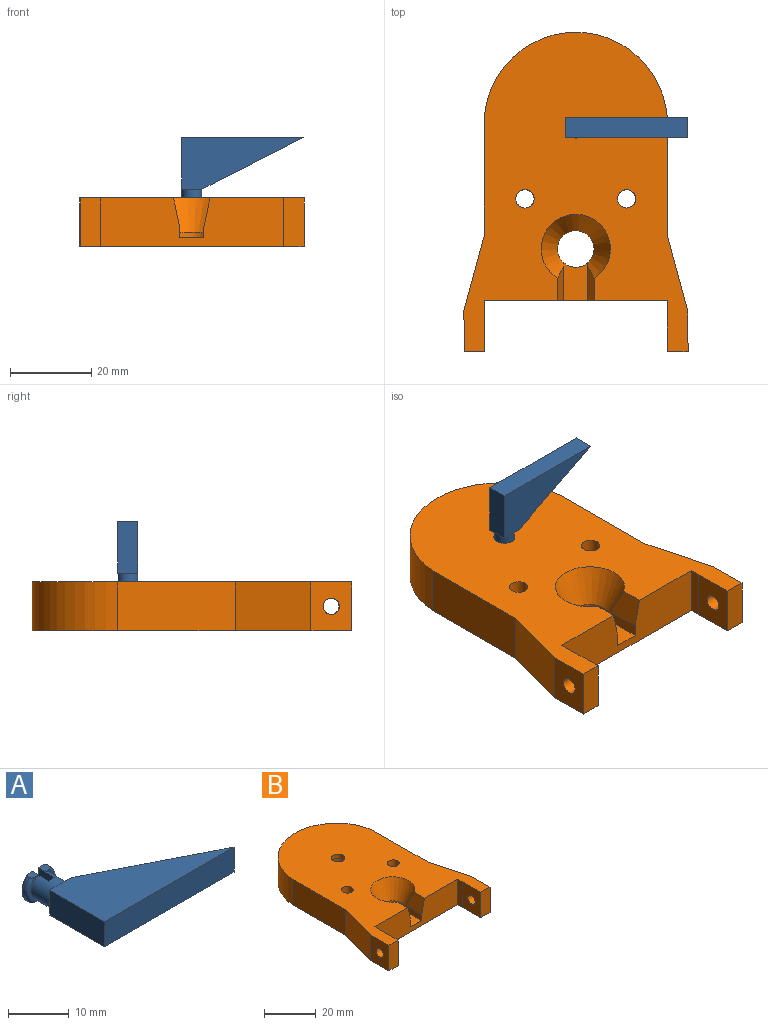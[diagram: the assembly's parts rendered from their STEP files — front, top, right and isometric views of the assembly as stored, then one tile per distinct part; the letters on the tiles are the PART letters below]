
ASSEMBLY  parts=2 mates=1
PART A: 27 faces, bbox 31.2x18.6x6.3 mm
  f0: plane 5x2.2mm, normal (0,1,0), area 8.9mm2, adj f7,f19,f21,f25
  f1: cylinder r=3.4mm len=5mm, axis (0,1,0), area 2.8mm2, adj f20,f22,f23,f24
  f2: plane 5x2.2mm, normal (0,-1,0), area 2.6mm2, adj f6,f8,f20,f22,f23
  f3: plane 5x2.2mm, normal (0,1,0), area 8.9mm2, adj f6,f20,f22,f24
  f4: cylinder r=3.4mm len=5mm, axis (0,1,0), area 2.8mm2, adj f19,f21,f25,f26
  f5: plane 5x2.2mm, normal (0,-1,0), area 2.6mm2, adj f7,f8,f19,f21,f26
  f6: plane 5x3.79mm, normal (1,0,0), area 18.5mm2, adj f2,f3,f8,f18,f20,f22
  f7: plane 5x3.79mm, normal (-1,0,0), area 18.5mm2, adj f0,f5,f8,f18,f19,f21
  f8: cylinder r=2.5mm len=5mm, axis (0,1,0), area 61mm2, adj f2,f5,f6,f7,f9,f10,f11,f12
  f9: plane 2.5x2.5mm, normal (0,1,0), area 1.3mm2, adj f8,f13,f16
  f10: plane 2.5x2.5mm, normal (0,1,0), area 1.3mm2, adj f8,f15,f16
  f11: plane 2.5x2.5mm, normal (0,1,0), area 1.3mm2, adj f8,f15,f17
  f12: plane 2.5x2.5mm, normal (0,1,0), area 1.3mm2, adj f8,f13,f17
  f13: plane 12.77x5mm, normal (-1,0,0), area 63.8mm2, adj f9,f12,f14,f16,f17
  f14: plane 30x5mm, normal (0,-1,0), area 150mm2, adj f13,f15,f16,f17
  f15: plane 25x12.77mm, normal (0.45,0.89,0), area 140.4mm2, adj f10,f11,f14,f16,f17
  f16: plane 30x12.77mm, normal (0,0,1), area 223.4mm2, adj f9,f10,f13,f14,f15
  f17: plane 30x12.77mm, normal (0,0,-1), area 223.4mm2, adj f11,f12,f13,f14,f15
  f18: plane 5x1.4mm, normal (0,1,0), area 6.9mm2, adj f6,f7,f8
  f19: plane 1.61x1.49mm, normal (0,0,1), area 2.2mm2, adj f0,f4,f5,f7,f25,f26
  f20: plane 1.61x1.49mm, normal (0,0,1), area 2.2mm2, adj f1,f2,f3,f6,f23,f24
  f21: plane 1.61x1.49mm, normal (0,0,-1), area 2.2mm2, adj f0,f4,f5,f7,f25,f26
  f22: plane 1.61x1.49mm, normal (0,0,-1), area 2.2mm2, adj f1,f2,f3,f6,f23,f24
  f23: torus R=2.9mm, axis (0,1,0), area 4.5mm2, adj f1,f2,f20,f22
  f24: torus R=2.9mm, axis (0,1,0), area 4.5mm2, adj f1,f3,f20,f22
  f25: torus R=2.9mm, axis (0,1,0), area 4.5mm2, adj f0,f4,f19,f21
  f26: torus R=2.9mm, axis (0,1,0), area 4.5mm2, adj f4,f5,f19,f21
PART B: 31 faces, bbox 55.2x78.6x12.1 mm
  f0: plane 28.92x12mm, normal (1,0,0), area 347mm2, adj f6,f7,f13,f15
  f1: plane 28.92x12mm, normal (-1,0,0), area 347mm2, adj f6,f7,f12,f15
  f2: plane 9.4x2.85mm, normal (1,0,0), area 25.5mm2, adj f3,f5,f8,f9,f16
  f3: cylinder r=4.5mm len=9mm, axis (0,0,-1), area 90.4mm2, adj f2,f4,f7,f8,f16
  f4: plane 9.4x2.85mm, normal (-1,0,0), area 25.5mm2, adj f3,f5,f8,f10,f16
  f5: plane 45x12mm, normal (0,-1,0), area 470.7mm2, adj f2,f4,f6,f7,f8,f9,f10,f11
  f6: plane 78.51x55.12mm, normal (0,0,1), area 2624.7mm2, adj f0,f1,f5,f9,f10,f11,f12,f13
  f7: plane 78.51x55.12mm, normal (0,0,-1), area 2850mm2, adj f0,f1,f3,f5,f11,f12,f13,f14
  f8: plane 9.35x6mm, normal (0,0,1), area 51.4mm2, adj f2,f3,f4,f5
  f9: plane 8.54x7.1mm, normal (0.98,0,0.21), area 49.9mm2, adj f2,f5,f6,f16
  f10: plane 8.54x7.1mm, normal (-0.98,0,0.21), area 49.9mm2, adj f4,f5,f6,f16
  f11: plane 12x2.5mm, normal (1,0,0), area 30mm2, adj f5,f6,f7,f18
  f12: plane 18.64x12mm, normal (-0.97,0.26,0), area 231.6mm2, adj f1,f6,f7,f17
  f13: plane 18.64x12mm, normal (0.97,0.26,0), area 231.6mm2, adj f0,f6,f7,f21
  f14: plane 12x2.5mm, normal (-1,0,0), area 30mm2, adj f5,f6,f7,f20
  f15: cylinder r=22.56mm len=45mm, axis (0,0,-1), area 812mm2, adj f0,f1,f6,f7
  f16: cone r=4.5mm half-angle=25.2deg, axis (0,0,1), area 311mm2, adj f2,f3,f4,f6,f9,f10
  f17: plane 12x10mm, normal (-1,-0.01,0), area 107.4mm2, adj f6,f7,f12,f19,f23
  f18: plane 12x10mm, normal (1,0.01,0), area 107.4mm2, adj f6,f7,f11,f19,f23
  f19: plane 12x5.01mm, normal (0.01,-1,0), area 60.1mm2, adj f6,f7,f17,f18
  f20: plane 12x10mm, normal (-1,-0.01,0), area 107.4mm2, adj f6,f7,f14,f22,f24
  f21: plane 12x10mm, normal (1,0.01,0), area 107.4mm2, adj f6,f7,f13,f22,f24
  f22: plane 12x5.01mm, normal (-0.01,-1,0), area 60.1mm2, adj f6,f7,f20,f21
  f23: cylinder r=2mm len=5.05mm, axis (1,0.01,0), area 62.9mm2, adj f17,f18
  f24: cylinder r=2mm len=5.05mm, axis (-1,-0.01,0), area 62.9mm2, adj f20,f21
  f25: cylinder r=2.25mm len=12mm, axis (0,0,-1), area 169.6mm2, adj f6,f7
  f26: cylinder r=2.25mm len=12mm, axis (0,0,-1), area 169.6mm2, adj f6,f7
  f27: cylinder r=2.55mm len=5.1mm, axis (0,0,1), area 32mm2, adj f6,f28
  f28: plane 7x7mm, normal (0,0,-1), area 18.1mm2, adj f27,f30
  f29: plane 7x7mm, normal (0,0,1), area 38.5mm2, adj f30
  f30: cylinder r=3.5mm len=7mm, axis (0,0,1), area 88mm2, adj f28,f29
PLACE A rot(axis=(-1,0,0),90deg) t=(5.37,22.79,27.86)mm
PLACE B t=(-1.47,2.79,5.71)mm
MATE revolute A.f1 <-> B.f27  axis (0,0,-1) through (-1.47,22.79,17.71)mm
